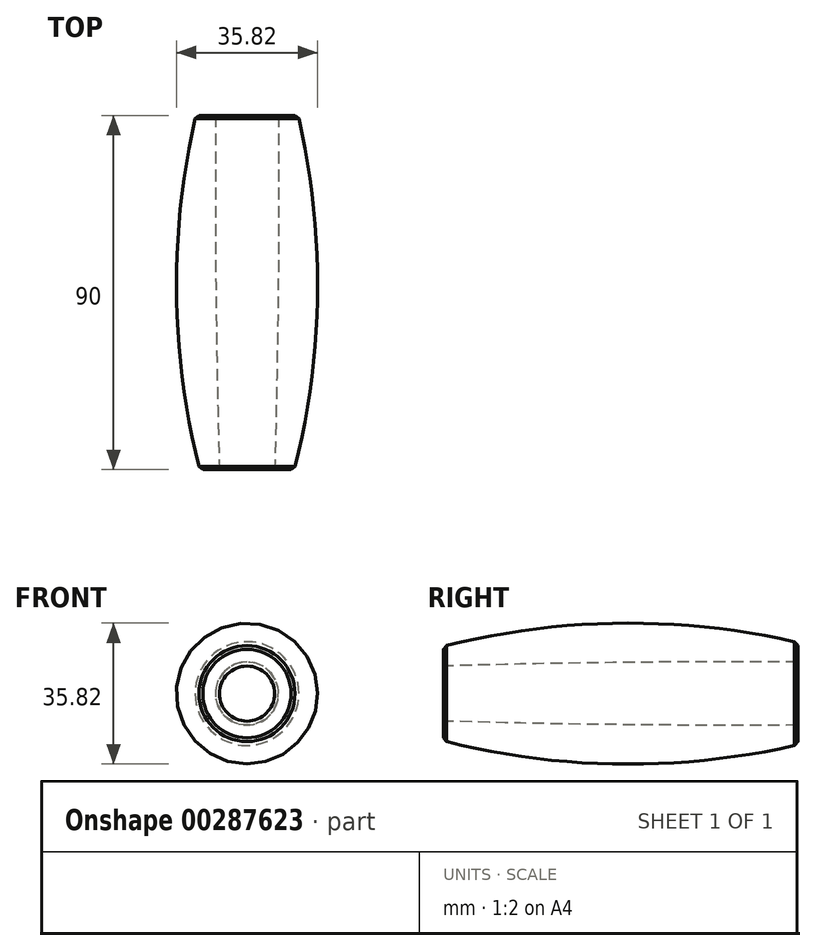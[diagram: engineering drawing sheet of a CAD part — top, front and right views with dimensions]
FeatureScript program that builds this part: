
annotation { "Feature Type Name" : "Feature", "Feature Type Description" : "" }
export const myFeature = defineFeature(function(context is Context, id is Id, definition is map)
    precondition{}
    {
        {
            var Q0;
            Q0=qCreatedBy(makeId("Top.planeOp"),FACE);
            var sketch = newSketch(context, id + "F0", { "sketchPlane" : qUnion([Q0])});
            skLineSegment(sketch, "E0", {"start": v(0, 45) * mm, "end": v(0, -45) * mm, "construction": true});
            skPoint(sketch, "E1", {"position": v(0, 0) * mm});
            skLineSegment(sketch, "E2", {"start": v(0, 45) * mm, "end": v(8, 45) * mm});
            skLineSegment(sketch, "E3", {"start": v(0, -45) * mm, "end": v(7, -45) * mm});
            skArc(sketch, "E4", {"start": v(7, -45) * mm, "mid": v(7.9, 0) * mm, "end": v(8, 45) * mm});
            skLineSegment(sketch, "E5", {"start": v(8, 45) * mm, "end": v(13, 45) * mm});
            skLineSegment(sketch, "E6", {"start": v(7, -45) * mm, "end": v(12, -45) * mm});
            skArc(sketch, "E7", {"start": v(12, -45) * mm, "mid": v(17.9, -0.06) * mm, "end": v(13, 45) * mm});
            skSolve(sketch);
        }
        {
            var Q0;
            Q0=makeQuery(id+"F0.imprint","IMPRINT",FACE,{"disambiguationData":[TD([[makeQuery(id+"F0.imprint","IMPRINT",EDGE,{"derivedFrom":sQuery(id+"F0.wireOp",EDGE,"E4")}),-1.0]])]});
            var Q1;
            Q1=sQuery(id+"F0.wireOp",EDGE,"E0");
            revolve(context, id + "F1", {"surfaceOperationType" : NewSurfaceOperationType.NEW, "entities" : qUnion([Q0]), "axis" : qUnion([Q1]), "revolveType" : RevolveType.FULL});
        }
        {
            var Q0;
            Q0=makeQuery(id+"F1.opRevolve","SWEPT_EDGE",EDGE,{"disambiguationData":[OSD([sQuery(id+"F0.wireOp",EDGE,"E6"),sQuery(id+"F0.wireOp",EDGE,"E7")])]});
            var Q1;
            Q1=makeQuery(id+"F1.opRevolve","SWEPT_EDGE",EDGE,{"disambiguationData":[OSD([sQuery(id+"F0.wireOp",EDGE,"E5"),sQuery(id+"F0.wireOp",EDGE,"E7")])]});
            chamfer(context, id + "F2", {"entities" : qUnion([Q0, Q1]), "width" : 1 * mm, "tangentPropagation" : true});
        }
    });
